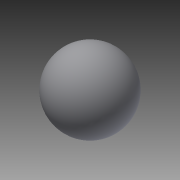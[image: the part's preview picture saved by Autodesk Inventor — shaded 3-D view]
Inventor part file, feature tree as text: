
AUTODESK INVENTOR PART (.ipt)
format: ipt  version: 2016 (Build 200138000, 138)  size: 102,400 bytes
history: native  units: in
note: dims shown in document units (in); Inventor stores cm internally (conversion verified against a paired STEP export)
features: plane x4, revolve x1, sketch x1
ambient origin geometry x8: Origin, YZ Plane, XZ Plane, XY Plane, X Axis, Y Axis, Z Axis, Center Point
bodies: Solid1 (feature_tree)
feature tree (6):
  revolve  "Revolution1"  Angle=90.0deg
  plane  "Work Plane2"
  plane  "Work Plane3"
  plane  "Work Plane5"
  sketch  "Sketch1"  dims[d0=10.0in d1=90.0deg d2=5.0in d3=-10.0in d4=5.0in d6=-5.0in]
  plane  "Work Plane1"
